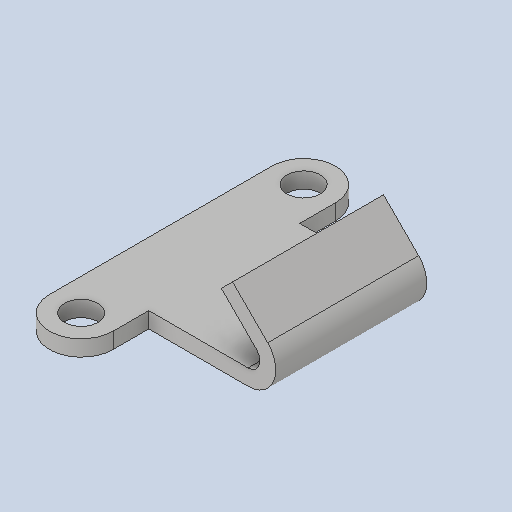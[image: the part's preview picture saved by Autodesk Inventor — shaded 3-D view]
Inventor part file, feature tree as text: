
AUTODESK INVENTOR PART (.ipt)
format: ipt  version: 2024.2 (Build 282272000, 272)  size: 137,216 bytes
history: native  units: mm
features: other x7, extrude x4, sketch x4
ambient origin geometry x8: Origin, YZ Plane, XZ Plane, XY Plane, X Axis, Y Axis, Z Axis, Center Point
bodies: Solid1 (feature_tree)
feature tree (15):
  extrude  "Extrusion1"  Depth=18.0mm TaperAngle=0.0deg
  extrude  "Extrusion2"  Depth=18.0mm TaperAngle=0.0deg
  extrude  "Extrusion3"  [1 undecoded]
  extrude  "Extrusion4"  [1 undecoded]
  other  "C_XY"
  other  "C_YZ"
  other  "C_ZX"
  other  "C_X"
  other  "C_Y"
  other  "C_Z"
  other  "C_Center"
  sketch  "Sketch_1"  dims[d0=18.0mm d1=0.0mm d2=18.0mm d3=0.0mm]
  sketch  "Sketch_2"  dims[d4=18.0mm d5=0.0mm d6=18.0mm d7=0.0mm]
  sketch  "Sketch_3"
  sketch  "Sketch_4"
note: 2 required parameter values undecoded (feature->parameter linkage not recoverable at this tier; creation-order binding heuristic only, values carry confidence <= 0.55)
